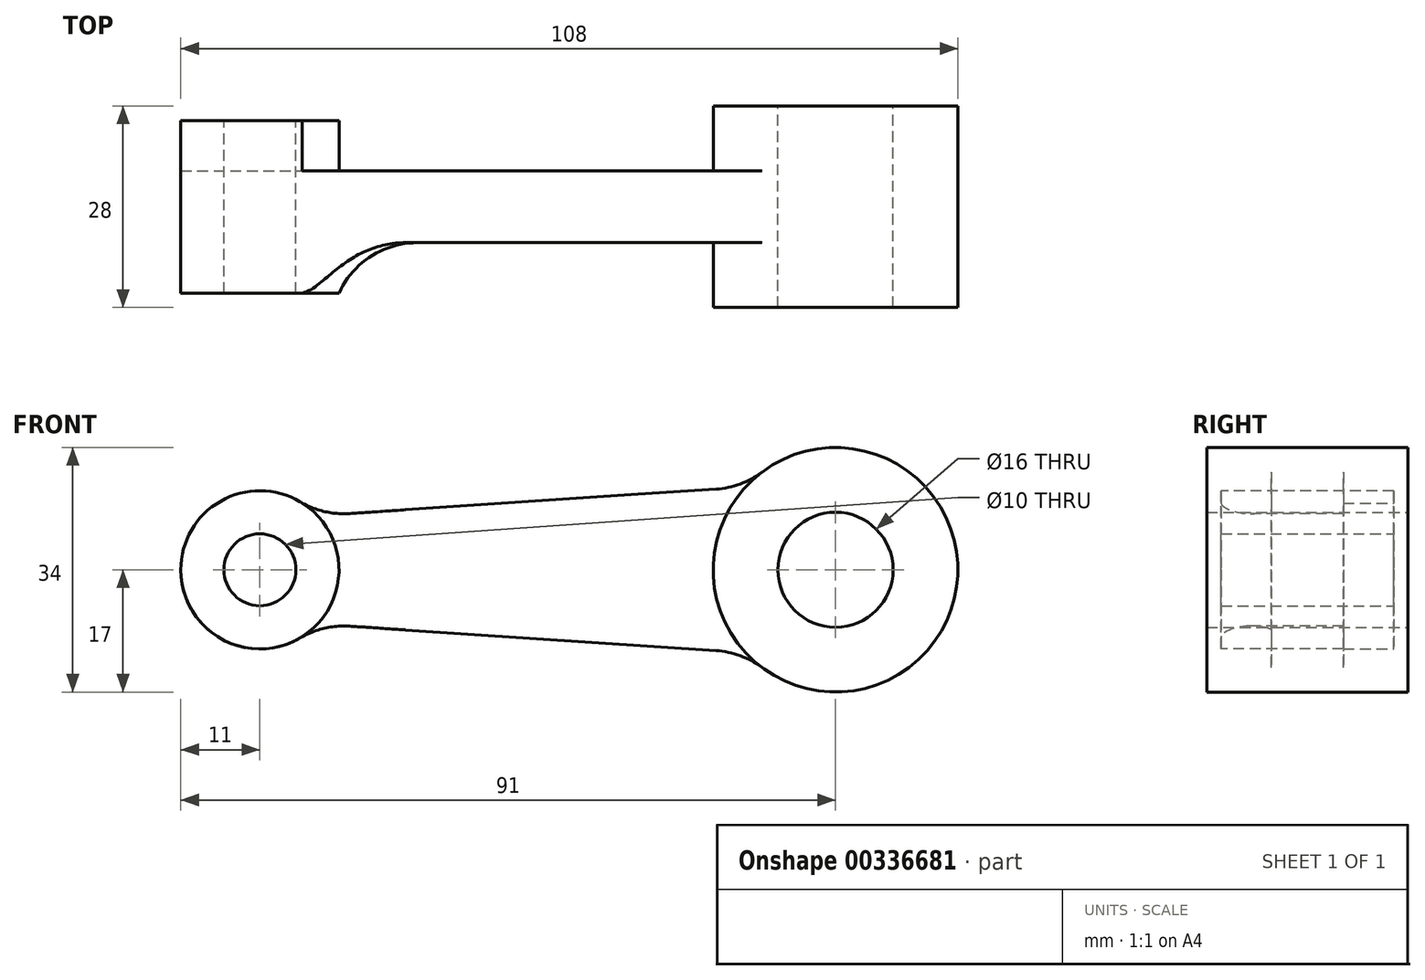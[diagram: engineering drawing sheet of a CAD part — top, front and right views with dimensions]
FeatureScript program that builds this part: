
annotation { "Feature Type Name" : "Feature", "Feature Type Description" : "" }
export const myFeature = defineFeature(function(context is Context, id is Id, definition is map)
    precondition{}
    {
        {
            var Q0;
            Q0=qCreatedBy(makeId("Front.planeOp"),FACE);
            var sketch = newSketch(context, id + "F0", { "sketchPlane" : qUnion([Q0])});
            skArc(sketch, "E0", {"start": v(-72.8, 37.3) * mm, "mid": v(-45.6, 50.9) * mm, "end": v(-72.8, 64.5) * mm});
            skCircle(sketch, "E1", {"center": v(-62.6, 50.9) * mm, "radius": 8 * mm});
            skLineSegment(sketch, "E2", {"start": v(-62.6, 50.9) * mm, "end": v(-142.6, 50.9) * mm});
            skArc(sketch, "E3", {"start": v(-137.01, 60.36) * mm, "mid": v(-153.6, 50.9) * mm, "end": v(-137.01, 41.42) * mm});
            skCircle(sketch, "E4", {"center": v(-142.6, 50.9) * mm, "radius": 5 * mm});
            skLineSegment(sketch, "E5", {"start": v(-142.6, 50.9) * mm, "end": v(-127.6, 50.9) * mm});
            skLineSegment(sketch, "E6", {"start": v(-62.6, 50.9) * mm, "end": v(-82.6, 50.9) * mm});
            skLineSegment(sketch, "E7", {"start": v(-82.6, 50.9) * mm, "end": v(-82.6, 61.9) * mm});
            skLineSegment(sketch, "E8", {"start": v(-82.6, 50.9) * mm, "end": v(-82.6, 39.9) * mm});
            skLineSegment(sketch, "E9", {"start": v(-127.6, 50.9) * mm, "end": v(-127.6, 42.9) * mm});
            skLineSegment(sketch, "E10", {"start": v(-127.6, 50.9) * mm, "end": v(-127.6, 58.9) * mm});
            skLineSegment(sketch, "E11", {"start": v(-127.6, 58.9) * mm, "end": v(-82.6, 61.9) * mm});
            skLineSegment(sketch, "E12", {"start": v(-90.02, 61.4) * mm, "end": v(-79.2, 62.12) * mm});
            skLineSegment(sketch, "E13", {"start": v(-90.02, 61.4) * mm, "end": v(-130.12, 58.72) * mm});
            skLineSegment(sketch, "E14", {"start": v(-82.6, 39.9) * mm, "end": v(-127.6, 42.9) * mm});
            skLineSegment(sketch, "E15", {"start": v(-127.6, 42.9) * mm, "end": v(-122.85, 42.57) * mm});
            skLineSegment(sketch, "E16", {"start": v(-122.85, 42.57) * mm, "end": v(-130.12, 43.06) * mm});
            skLineSegment(sketch, "E17", {"start": v(-122.85, 42.57) * mm, "end": v(-79.2, 39.66) * mm});
            skPoint(sketch, "E18.visualSharp", {"position": v(-75.13, 62.39) * mm});
            skArc(sketch, "E18.filletArc", {"start": v(-79.2, 62.12) * mm, "mid": v(-75.83, 62.84) * mm, "end": v(-72.8, 64.5) * mm});
            skPoint(sketch, "E19.visualSharp", {"position": v(-75.13, 39.4) * mm});
            skArc(sketch, "E19.filletArc", {"start": v(-72.8, 37.3) * mm, "mid": v(-75.83, 38.94) * mm, "end": v(-79.2, 39.66) * mm});
            skPoint(sketch, "E20.visualSharp", {"position": v(-134.6, 43.36) * mm});
            skArc(sketch, "E20.filletArc", {"start": v(-130.12, 43.06) * mm, "mid": v(-133.69, 42.76) * mm, "end": v(-137.01, 41.42) * mm});
            skPoint(sketch, "E21.visualSharp", {"position": v(-134.6, 58.42) * mm});
            skArc(sketch, "E21.filletArc", {"start": v(-137.01, 60.36) * mm, "mid": v(-133.69, 59.02) * mm, "end": v(-130.12, 58.72) * mm});
            skCircle(sketch, "E22", {"center": v(-142.6, 50.9) * mm, "radius": 11 * mm});
            skCircle(sketch, "E23", {"center": v(-62.6, 50.9) * mm, "radius": 17 * mm});
            skSolve(sketch);
        }
        {
            var Q0;
            Q0=makeQuery(id+"F0.imprint","IMPRINT",FACE,{"disambiguationData":[TD([[makeQuery(id+"F0.imprint","IMPRINT",EDGE,{"derivedFrom":sQuery(id+"F0.wireOp",EDGE,"E4")}),-1.0]])]});
            extrude(context, id + "F1", {"entities" : qUnion([Q0]), "depth" : 12 * mm});
        }
        {
            var Q0;
            Q0=makeQuery(id+"F0.imprint","IMPRINT",FACE,{"disambiguationData":[TD([[makeQuery(id+"F0.imprint","IMPRINT",EDGE,{"derivedFrom":sQuery(id+"F0.wireOp",EDGE,"E1")}),-1.0]])]});
            extrude(context, id + "F2", {"entities" : qUnion([Q0]), "depth" : 14 * mm});
        }
        {
            var Q0;
            Q0=makeQuery(id+"F2.opExtrude","CAP_FACE",FACE,{"disambiguationData":[OSD([sQuery(id+"F0.wireOp",EDGE,"E1"),sQuery(id+"F0.wireOp",EDGE,"E23")])],"isStart":false});
            extrude(context, id + "F3", {"entities" : qUnion([Q0]), "operationType" : NewBodyOperationType.ADD, "oppositeDirection" : true, "depth" : 28 * mm});
        }
        {
            var Q0;
            Q0=makeQuery(id+"F1.opExtrude","CAP_FACE",FACE,{"disambiguationData":[OSD([sQuery(id+"F0.wireOp",EDGE,"E4"),sQuery(id+"F0.wireOp",EDGE,"E22")])],"isStart":false});
            extrude(context, id + "F4", {"entities" : qUnion([Q0]), "operationType" : NewBodyOperationType.ADD, "oppositeDirection" : true, "depth" : 24 * mm});
        }
        {
            var Q0;
            Q0=makeQuery(id+"F0.imprint","IMPRINT",FACE,{"disambiguationData":[TD([[makeQuery(id+"F0.imprint","IMPRINT",EDGE,{"derivedFrom":sQuery(id+"F0.wireOp",EDGE,"E2")}),-1.0]])]});
            var Q1;
            Q1=makeQuery(id+"F0.imprint","IMPRINT",FACE,{"disambiguationData":[TD([[makeQuery(id+"F0.imprint","IMPRINT",EDGE,{"derivedFrom":sQuery(id+"F0.wireOp",EDGE,"E2")}),1.0]])]});
            var Q2;
            {var subQ2=sQuery(id+"F0.wireOp",EDGE,"E7");Q2=makeQuery(id+"F0.imprint","IMPRINT",FACE,{"disambiguationData":[TD([[makeQuery(id+"F0.imprint","IMPRINT",EDGE,{"derivedFrom":subQ2}),-1.0]])]});}
            var Q3;
            {var subQ2=sQuery(id+"F0.wireOp",EDGE,"E8");Q3=makeQuery(id+"F0.imprint","IMPRINT",FACE,{"disambiguationData":[TD([[makeQuery(id+"F0.imprint","IMPRINT",EDGE,{"derivedFrom":subQ2}),1.0]])]});}
            var Q4;
            {var subQ2=sQuery(id+"F0.wireOp",EDGE,"E9");Q4=makeQuery(id+"F0.imprint","IMPRINT",FACE,{"disambiguationData":[TD([[makeQuery(id+"F0.imprint","IMPRINT",EDGE,{"derivedFrom":subQ2}),-1.0]])]});}
            var Q5;
            {var subQ2=sQuery(id+"F0.wireOp",EDGE,"E10");Q5=makeQuery(id+"F0.imprint","IMPRINT",FACE,{"disambiguationData":[TD([[makeQuery(id+"F0.imprint","IMPRINT",EDGE,{"derivedFrom":subQ2}),1.0]])]});}
            extrude(context, id + "F5", {"entities" : qUnion([Q0, Q1, Q2, Q3, Q4, Q5]), "depth" : 5 * mm});
        }
        {
            var Q0;
            Q0=makeQuery(id+"F5.opExtrude","CAP_FACE",FACE,{"disambiguationData":[OSD([sQuery(id+"F0.wireOp",EDGE,"E12"),sQuery(id+"F0.wireOp",EDGE,"E13"),sQuery(id+"F0.wireOp",EDGE,"E16"),sQuery(id+"F0.wireOp",EDGE,"E17"),sQuery(id+"F0.wireOp",EDGE,"E18.filletArc"),sQuery(id+"F0.wireOp",EDGE,"E19.filletArc"),sQuery(id+"F0.wireOp",EDGE,"E20.filletArc"),sQuery(id+"F0.wireOp",EDGE,"E21.filletArc"),sQuery(id+"F0.wireOp",EDGE,"E22"),sQuery(id+"F0.wireOp",EDGE,"E23")])],"isStart":false});
            extrude(context, id + "F6", {"entities" : qUnion([Q0]), "oppositeDirection" : true, "depth" : 10 * mm});
        }
        {
            var Q0;
            Q0=makeQuery(id+"F6.opExtrude","SWEPT_BODY",BODY,{"disambiguationData":[OSD([sQuery(id+"F0.wireOp",EDGE,"E12"),sQuery(id+"F0.wireOp",EDGE,"E13"),sQuery(id+"F0.wireOp",EDGE,"E16"),sQuery(id+"F0.wireOp",EDGE,"E17"),sQuery(id+"F0.wireOp",EDGE,"E18.filletArc"),sQuery(id+"F0.wireOp",EDGE,"E19.filletArc"),sQuery(id+"F0.wireOp",EDGE,"E20.filletArc"),sQuery(id+"F0.wireOp",EDGE,"E21.filletArc"),sQuery(id+"F0.wireOp",EDGE,"E22"),sQuery(id+"F0.wireOp",EDGE,"E23")])]});
            var Q1;
            Q1=makeQuery(id+"F2.opExtrude","SWEPT_BODY",BODY,{"disambiguationData":[OSD([sQuery(id+"F0.wireOp",EDGE,"E1"),sQuery(id+"F0.wireOp",EDGE,"E23")])]});
            var Q2;
            Q2=makeQuery(id+"F5.opExtrude","SWEPT_BODY",BODY,{"disambiguationData":[OSD([sQuery(id+"F0.wireOp",EDGE,"E12"),sQuery(id+"F0.wireOp",EDGE,"E13"),sQuery(id+"F0.wireOp",EDGE,"E16"),sQuery(id+"F0.wireOp",EDGE,"E17"),sQuery(id+"F0.wireOp",EDGE,"E18.filletArc"),sQuery(id+"F0.wireOp",EDGE,"E19.filletArc"),sQuery(id+"F0.wireOp",EDGE,"E20.filletArc"),sQuery(id+"F0.wireOp",EDGE,"E21.filletArc"),sQuery(id+"F0.wireOp",EDGE,"E22"),sQuery(id+"F0.wireOp",EDGE,"E23")])]});
            var Q3;
            Q3=makeQuery(id+"F1.opExtrude","SWEPT_BODY",BODY,{"disambiguationData":[OSD([sQuery(id+"F0.wireOp",EDGE,"E4"),sQuery(id+"F0.wireOp",EDGE,"E22")])]});
            booleanBodies(context, id + "F7", {"operationType" : BooleanOperationType.UNION, "tools" : qUnion([Q0, Q1, Q2, Q3])});
        }
        {
            var Q0;
            {var subQ0=sQuery(id+"F0.wireOp",EDGE,"E23");Q0=makeQuery(id+"F7.opBoolean","MERGE",EDGE,{"derivedFrom":[makeQuery(id+"F5.opExtrude","CAP_EDGE",EDGE,{"disambiguationData":[OSD([subQ0])],"isStart":false}),makeQuery(id+"F6.opExtrude","CAP_EDGE",EDGE,{"disambiguationData":[OSD([subQ0])],"isStart":true})]});}
            var Q1;
            Q1=makeQuery(id+"F6.opExtrude","CAP_EDGE",EDGE,{"disambiguationData":[OSD([sQuery(id+"F0.wireOp",EDGE,"E23")])],"isStart":false});
            var Q2;
            {var subQ0=sQuery(id+"F0.wireOp",EDGE,"E22");Q2=makeQuery(id+"F7.opBoolean","MERGE",EDGE,{"derivedFrom":[makeQuery(id+"F5.opExtrude","CAP_EDGE",EDGE,{"disambiguationData":[OSD([subQ0])],"isStart":false}),makeQuery(id+"F6.opExtrude","CAP_EDGE",EDGE,{"disambiguationData":[OSD([subQ0])],"isStart":true})]});}
            var Q3;
            Q3=makeQuery(id+"F6.opExtrude","CAP_EDGE",EDGE,{"disambiguationData":[OSD([sQuery(id+"F0.wireOp",EDGE,"E22")])],"isStart":false});
            fillet(context, id + "F8", {"entities" : qUnion([Q0, Q1, Q2, Q3]), "radius" : 12 * mm, "tangentPropagation" : true, "allowEdgeOverflow" : false});
        }
    });
